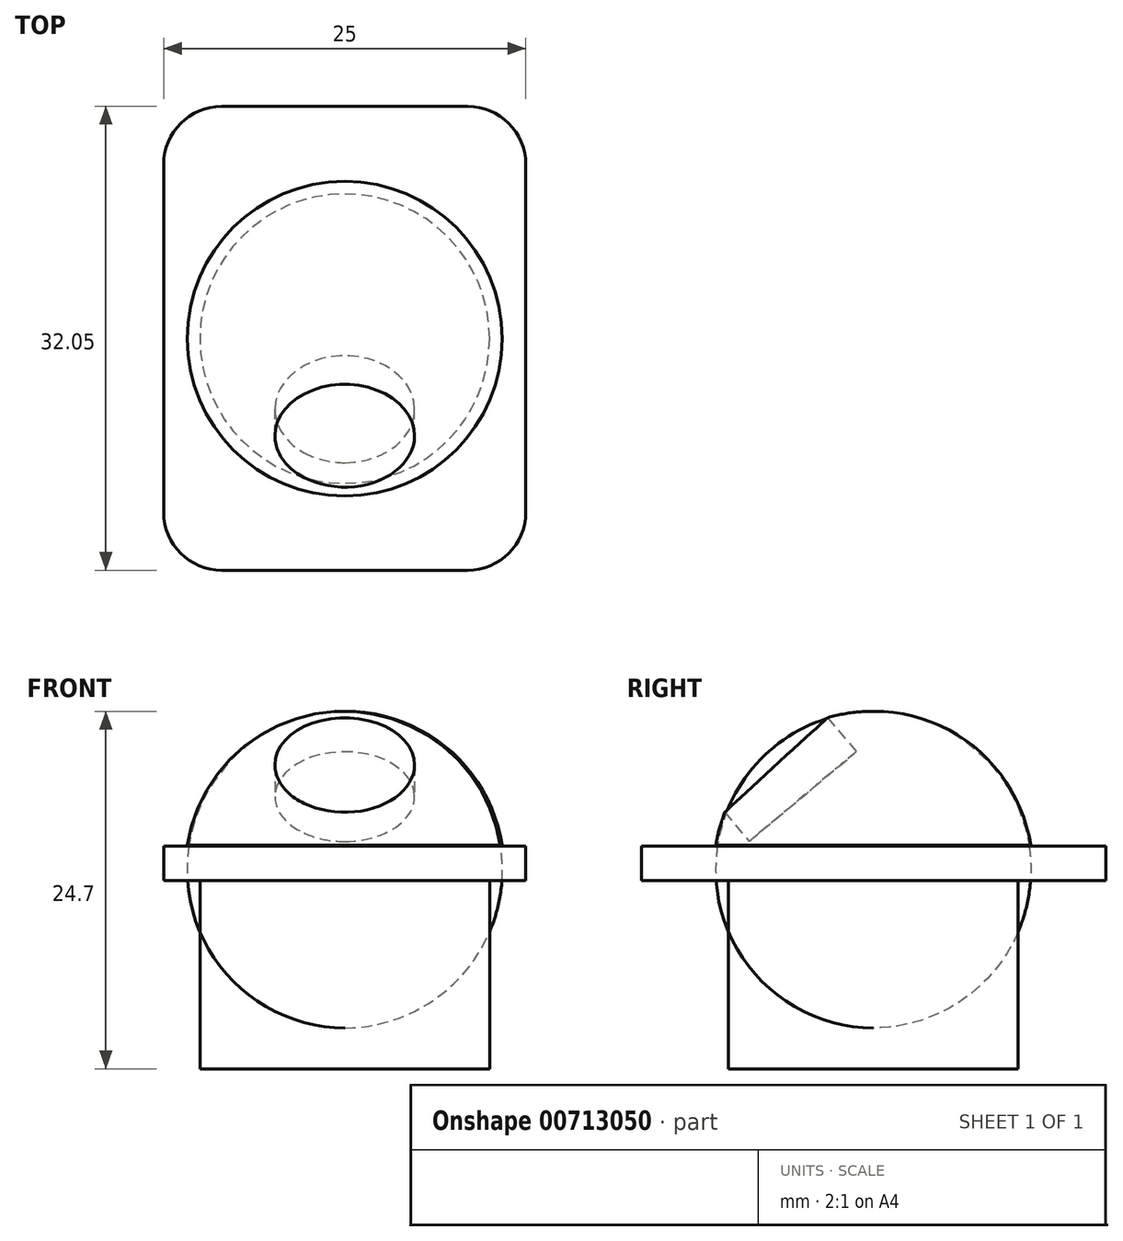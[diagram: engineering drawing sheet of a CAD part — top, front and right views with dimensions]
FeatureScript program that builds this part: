
annotation { "Feature Type Name" : "Feature", "Feature Type Description" : "" }
export const myFeature = defineFeature(function(context is Context, id is Id, definition is map)
    precondition{}
    {
        {
            var Q0;
            Q0=qCreatedBy(makeId("Top.planeOp"),FACE);
            var sketch = newSketch(context, id + "F0", { "sketchPlane" : qUnion([Q0])});
            skCircle(sketch, "E0", {"center": v(0, 0) * mm, "radius": 10 * mm});
            skSolve(sketch);
        }
        {
            var Q0;
            Q0=makeQuery(id+"F0.imprint","IMPRINT",FACE,{"disambiguationData":[TD([[makeQuery(id+"F0.imprint","IMPRINT",EDGE,{"derivedFrom":sQuery(id+"F0.wireOp",EDGE,"E0")}),1.0]])]});
            extrude(context, id + "F1", {"entities" : qUnion([Q0]), "oppositeDirection" : true, "depth" : 13 * mm, "offsetDistance" : 25 * mm});
        }
        {
            var Q0;
            Q0=makeQuery(id+"F1.opExtrude","CAP_FACE",FACE,{"disambiguationData":[OSD([sQuery(id+"F0.wireOp",EDGE,"E0")])],"isStart":true});
            var sketch = newSketch(context, id + "F2", { "sketchPlane" : qUnion([Q0])});
            skLineSegment(sketch, "E1", {"start": v(0, 0) * mm, "end": v(0, -16) * mm, "construction": true});
            skLineSegment(sketch, "E2", {"start": v(0, -16) * mm, "end": v(0, 16.05) * mm, "construction": true});
            skPoint(sketch, "E3.middle", {"position": v(0, 3.37) * mm});
            skLineSegment(sketch, "E4", {"start": v(-12.5, 16.05) * mm, "end": v(12.5, 16.05) * mm});
            skLineSegment(sketch, "E5", {"start": v(-12.5, -16) * mm, "end": v(12.5, -16) * mm});
            skLineSegment(sketch, "E6", {"start": v(12.5, 16.05) * mm, "end": v(12.5, -16) * mm});
            skLineSegment(sketch, "E7", {"start": v(-12.5, 16.05) * mm, "end": v(-12.5, -16) * mm});
            skSolve(sketch);
        }
        {
            var Q0;
            Q0=makeQuery(id+"F2.imprint","IMPRINT",FACE,{"disambiguationData":[TD([[makeQuery(id+"F2.imprint","IMPRINT",EDGE,{"derivedFrom":sQuery(id+"F2.wireOp",EDGE,"E4")}),-1.0]])]});
            var Q1;
            Q1=makeQuery(id+"F2.imprint","IMPRINT",FACE,{"disambiguationData":[TD([[makeQuery(id+"F2.imprint","IMPRINT",EDGE,{"derivedFrom":makeQuery(id+"F1.opExtrude","CAP_EDGE",EDGE,{"disambiguationData":[OSD([sQuery(id+"F0.wireOp",EDGE,"E0")])],"isStart":true})}),1.0]])]});
            extrude(context, id + "F3", {"entities" : qUnion([Q0, Q1]), "operationType" : NewBodyOperationType.ADD, "depth" : 2.4 * mm, "offsetDistance" : 25 * mm});
        }
        {
            var Q0;
            Q0=makeQuery(id+"F3.opExtrude","SWEPT_EDGE",EDGE,{"disambiguationData":[OSD([sQuery(id+"F2.wireOp",EDGE,"E5"),sQuery(id+"F2.wireOp",EDGE,"E7")])]});
            var Q1;
            Q1=makeQuery(id+"F3.opExtrude","SWEPT_EDGE",EDGE,{"disambiguationData":[OSD([sQuery(id+"F2.wireOp",EDGE,"E5"),sQuery(id+"F2.wireOp",EDGE,"E6")])]});
            var Q2;
            Q2=makeQuery(id+"F3.opExtrude","SWEPT_EDGE",EDGE,{"disambiguationData":[OSD([sQuery(id+"F2.wireOp",EDGE,"E4"),sQuery(id+"F2.wireOp",EDGE,"E6")])]});
            var Q3;
            Q3=makeQuery(id+"F3.opExtrude","SWEPT_EDGE",EDGE,{"disambiguationData":[OSD([sQuery(id+"F2.wireOp",EDGE,"E4"),sQuery(id+"F2.wireOp",EDGE,"E7")])]});
            fillet(context, id + "F4", {"entities" : qUnion([Q0, Q1, Q2, Q3]), "radius" : 4 * mm, "tangentPropagation" : true, "allowEdgeOverflow" : false});
        }
        {
            var Q0;
            Q0=qCreatedBy(makeId("Front.planeOp"),FACE);
            var sketch = newSketch(context, id + "F5", { "sketchPlane" : qUnion([Q0])});
            skLineSegment(sketch, "E8", {"start": v(10.87, 2.44) * mm, "end": v(0, 2.44) * mm});
            skLineSegment(sketch, "E9", {"start": v(0, 2.44) * mm, "end": v(0, 11.7) * mm});
            skArc(sketch, "E10", {"start": v(10.87, 2.44) * mm, "mid": v(7.15, 9.1) * mm, "end": v(0, 11.7) * mm});
            skLineSegment(sketch, "E11", {"start": v(0, 2.44) * mm, "end": v(0, 14.36) * mm, "construction": true});
            skSolve(sketch);
        }
        {
            var Q0;
            Q0=makeQuery(id+"F5.imprint","IMPRINT",FACE,{"disambiguationData":[TD([[makeQuery(id+"F5.imprint","IMPRINT",EDGE,{"derivedFrom":sQuery(id+"F5.wireOp",EDGE,"E8")}),-1.0]])]});
            var Q1;
            Q1=sQuery(id+"F5.wireOp",EDGE,"E11");
            revolve(context, id + "F6", {"operationType" : NewBodyOperationType.ADD, "surfaceOperationType" : NewSurfaceOperationType.NEW, "entities" : qUnion([Q0]), "axis" : qUnion([Q1]), "revolveType" : RevolveType.FULL});
        }
        {
            var Q0;
            Q0=qCreatedBy(makeId("Right.planeOp"),FACE);
            var sketch = newSketch(context, id + "F7", { "sketchPlane" : qUnion([Q0])});
            skLineSegment(sketch, "E12", {"start": v(0, 0) * mm, "end": v(-11.8, 0) * mm, "construction": true});
            skLineSegment(sketch, "E13", {"start": v(-11.8, 0) * mm, "end": v(2.14, 11.7) * mm, "construction": true});
            skSolve(sketch);
        }
        {
            var Q0;
            Q0=sQuery(id+"F7.wireOp",EDGE,"E13");
            cPlane(context, id + "F8", {"entities" : qUnion([Q0]), "cplaneType" : CPlaneType.LINE_ANGLE, "offset" : 25 * mm, "angle" : 0 * degree, "oppositeDirection" : true, "width" : 150 * mm, "height" : 150 * mm});
        }
        {
            var Q0;
            Q0=qCreatedBy(id+"F8.planeOp",FACE);
            var sketch = newSketch(context, id + "F9", { "sketchPlane" : qUnion([Q0])});
            skCircle(sketch, "E14", {"center": v(0, 0) * mm, "radius": 4.82 * mm});
            skSolve(sketch);
        }
        {
            var Q0;
            Q0 = qSketchRegion(id + "F9", true);
            extrude(context, id + "F10", {"entities" : qUnion([Q0]), "operationType" : NewBodyOperationType.REMOVE, "endBound" : BoundingType.UP_TO_NEXT, "depth" : 25 * mm, "offsetDistance" : 1 * mm});
        }
    });
